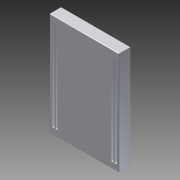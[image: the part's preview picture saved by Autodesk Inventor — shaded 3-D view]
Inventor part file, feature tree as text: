
AUTODESK INVENTOR PART (.ipt)
format: ipt  version: 2012 (Build 160160000, 160)  size: 202,752 bytes
history: native  units: in
note: dims shown in document units (in); Inventor stores cm internally (conversion verified against a paired STEP export)
features: extrude x2, fillet x2, sketch x1
ambient origin geometry x8: Origin, YZ Plane, XZ Plane, XY Plane, X Axis, Y Axis, Z Axis, Center Point
bodies: Solid1 (feature_tree)
feature tree (5):
  sketch  "Sketch1"  dims[d0=3.2283in d1=2.1654in d2=0.689in d3=1.3976in d4=0.4528in d5=0.0984in d6=0.0394in d7=0.3937in d8=1.0825in d9=0.3543in d10=0.3937in d11=0.2362in d12=0.9in d13=0.7569in d14=0.1in d15=0.027in d16=0.3937in d17=0.1in d18=0.02in d19=0.177in d20=0.177in d21=0.1in d22=0.177in d23=0.02in d24=0.1181in d25=0.0591in d26=0.2953in d27=0.0787in d28=0.0591in d29=0.0591in d30=0.0591in d31=0.0591in d32=0.0591in d33=0.0591in d34=0.0591in d35=0.1in d36=0.1in d37=0.1in d38=0.1in d39=0.1in d40=0.1in d41=0.1in d42=0.0591in d43=0.0591in d44=0.0591in d45=0.0591in d46=0.0591in d47=0.0591in d48=0.0591in d49=0.0591in d50=0.1in d51=0.1in d52=0.1in d53=0.1in d54=0.1in d55=0.1in d56=0.1in d57=0.0787in d58=0.2953in d59=0.0787in d60=0.0787in d61=0.0787in d62=0.0787in d63=0.0787in d64=0.0787in d65=0.0787in d66=0.1969in d67=0.1969in d68=0.1969in d69=0.1969in d70=0.0591in d71=0.0591in d72=0.1969in d73=0.1969in d74=0.0591in d75=0.0591in d76=0.0787in d77=0.0787in d78=0.1969in d79=0.1969in d80=0.1in d81=0.1in d82=0.1969in d83=0.1969in d84=0.1575in d85=0.1in d86=0.1969in d87=0.1969in d88=0.1969in d89=0.1969in d90=0.1969in d91=0.1969in d92=0.1969in d93=0.1969in d94=0.1181in d95=0.1181in d96=0.0394in d97=0.0394in d98=0.0394in d99=0.0394in d100=0.3543in d101=0.0in d102=0.315in d103=0.0in d104=0.005in d105=0.02in]
  extrude  "Extrusion1"  Depth=0.3543in TaperAngle=0.0deg
  extrude  "Extrusion2"  Depth=0.315in TaperAngle=0.0deg
  fillet  "Fillet1"  Radius=0.005in
  fillet  "Fillet2"  Radius=0.02in
